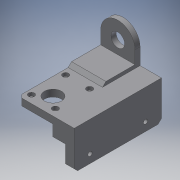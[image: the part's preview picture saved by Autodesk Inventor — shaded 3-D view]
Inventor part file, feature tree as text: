
AUTODESK INVENTOR PART (.ipt)
format: ipt  version: 2017 (Build 210142000, 142)  size: 240,128 bytes
history: native  units: mm
features: extrude x9, sketch x9, projected_geometry x4, reference x2, other x2, chamfer x1
ambient origin geometry x8: Origin, YZ Plane, XZ Plane, XY Plane, X Axis, Y Axis, Z Axis, Center Point
bodies: Solid1 (feature_tree)
feature tree (27):
  extrude  "Extrusion1"  Depth=40.0mm
  extrude  "Extrusion2"  Depth=20.0mm
  extrude  "Extrusion3"  Depth=40.12mm
  extrude  "Extrusion4"  Depth=8.0mm TaperAngle=0.0deg
  extrude  "Extrusion5"  Depth=4.0mm TaperAngle=0.0deg
  extrude  "Extrusion6"  Depth=40.0mm TaperAngle=0.0deg
  extrude  "Extrusion7"  Depth=16.0mm
  extrude  "Extrusion8"  TaperAngle=60.0deg  [1 undecoded]
  chamfer  "Chamfer1"  Distance=25.0mm
  extrude  "Extrusion9"  Depth=10.0mm TaperAngle=0.0deg
  sketch  "Sketch1"  dims[d0=28.0mm d1=40.0mm]
  sketch  "Sketch2"  dims[d2=20.0mm d3=4.5mm]
  projected_geometry  "Projected Loop1"
  sketch  "Sketch3"  dims[d4=58.1mm d5=40.12mm]
  sketch  "Sketch4"  dims[d6=37.9mm d7=8.0mm d8=0.0mm]
  reference  "Reference1"
  projected_geometry  "Projected Loop2"
  sketch  "Sketch5"  dims[d9=7.0mm d10=4.0mm d11=0.0mm]
  sketch  "Sketch6"  dims[d12=12.0mm d13=40.0mm d14=0.0mm]
  projected_geometry  "Projected Loop3"
  sketch  "Sketch7"  dims[d15=27.0mm d16=16.0mm]
  sketch  "Sketch8"  dims[d17=6.0mm d18=0.0mm d19=60.0deg]
  projected_geometry  "Projected Loop4"
  sketch  "Sketch9"  dims[d20=25.0mm d21=25.0mm d22=10.0mm d23=0.0mm d24=10.0mm d25=0.0mm d26=20.0mm d27=10.0mm d28=0.0mm d29=65.0mm d30=5.0mm d31=10.0mm d32=0.0mm d33=4.0mm d34=2.0mm d35=45.0deg d36=1.0mm d37=10.0mm d38=0.0mm]
  reference  "Reference2"
  other  "circulation pump.iam"
  other  "motor:1"
note: 1 required parameter value undecoded (feature->parameter linkage not recoverable at this tier; creation-order binding heuristic only, values carry confidence <= 0.55)
